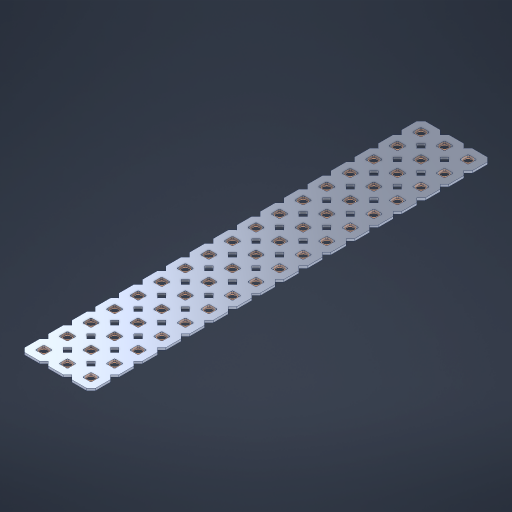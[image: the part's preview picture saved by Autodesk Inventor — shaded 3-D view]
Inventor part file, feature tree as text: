
AUTODESK INVENTOR PART (.ipt)
format: ipt  version: 2023 (Build 270158000, 158)  size: 847,872 bytes
history: native  units: in
note: dims shown in document units (in); Inventor stores cm internally (conversion verified against a paired STEP export)
features: other x52, extrude x50, sketch x2, pattern_linear x1
ambient origin geometry x8: Origin, YZ Plane, XZ Plane, XY Plane, X Axis, Y Axis, Z Axis, Center Point
bodies: Solid1 (feature_tree), Body (feature_tree)
feature tree (105):
  pattern_linear  "Rectangular Pattern1"  Spacing1=0.09in  [1 undecoded]
  sketch  "Sketch1"  dims[d1=0.5in]
  sketch  "Sketch2"  dims[d2=0.182in d3=0.09in d4=0.09in d5=0.09in d6=0.09in d7=0.09in d8=0.09in d9=0.09in d10=0.09in d11=0.02in d13=0.0in d14=0.172in d15=0.0625in d16=0.0in d19=0.5in d22=0.5in]
  other  "Srf1"
  other  "Srf126"
  other  "Srf127"
  other  "Srf128"
  other  "Srf129"
  other  "Srf130"
  other  "Srf131"
  other  "Srf250"
  other  "Srf251"
  other  "Srf252"
  other  "Srf253"
  other  "Srf254"
  other  "Srf255"
  other  "Srf256"
  other  "Srf257"
  other  "Srf258"
  other  "Srf259"
  other  "Srf268"
  other  "Srf269"
  other  "Srf270"
  other  "Srf271"
  other  "Srf272"
  other  "Srf273"
  other  "Srf274"
  other  "Srf275"
  other  "Srf276"
  other  "Srf277"
  other  "Srf278"
  other  "Srf279"
  other  "Srf280"
  other  "Srf281"
  other  "Srf282"
  other  "Srf283"
  other  "Srf284"
  other  "Srf293"
  other  "Srf294"
  other  "Srf295"
  other  "Srf296"
  other  "Srf297"
  other  "Srf298"
  other  "Srf299"
  other  "Srf300"
  other  "Srf301"
  other  "Srf302"
  other  "Srf303"
  other  "Srf304"
  other  "Srf305"
  other  "Srf306"
  other  "Srf307"
  other  "Srf308"
  other  "Srf309"
  other  "Circle"
  extrude  "ExtrusionSrf126"  Depth=0.09in
  extrude  "ExtrusionSrf127"  Depth=0.09in
  extrude  "ExtrusionSrf128"  Depth=0.09in
  extrude  "ExtrusionSrf129"  Depth=0.09in
  extrude  "ExtrusionSrf130"  Depth=0.09in
  extrude  "ExtrusionSrf131"  Depth=0.09in
  extrude  "ExtrusionSrf250"  Depth=0.09in
  extrude  "ExtrusionSrf251"  Depth=0.02in
  extrude  "ExtrusionSrf252"  TaperAngle=0.0deg  [1 undecoded]
  extrude  "ExtrusionSrf253"  Depth=0.5in
  extrude  "ExtrusionSrf254"  Depth=0.5in TaperAngle=0.0deg
  extrude  "ExtrusionSrf255"  Depth=0.5in
  extrude  "ExtrusionSrf256"  Depth=0.5in
  extrude  "ExtrusionSrf257"  [1 undecoded]
  extrude  "ExtrusionSrf258"  [1 undecoded]
  extrude  "ExtrusionSrf259"  [1 undecoded]
  extrude  "ExtrusionSrf268"  [1 undecoded]
  extrude  "ExtrusionSrf269"  [1 undecoded]
  extrude  "ExtrusionSrf270"  [1 undecoded]
  extrude  "ExtrusionSrf271"  [1 undecoded]
  extrude  "ExtrusionSrf272"  [1 undecoded]
  extrude  "ExtrusionSrf273"  [1 undecoded]
  extrude  "ExtrusionSrf274"  [1 undecoded]
  extrude  "ExtrusionSrf275"  [1 undecoded]
  extrude  "ExtrusionSrf276"  [1 undecoded]
  extrude  "ExtrusionSrf277"  [1 undecoded]
  extrude  "ExtrusionSrf278"  [1 undecoded]
  extrude  "ExtrusionSrf279"  [1 undecoded]
  extrude  "ExtrusionSrf280"  [1 undecoded]
  extrude  "ExtrusionSrf281"  [1 undecoded]
  extrude  "ExtrusionSrf282"  [1 undecoded]
  extrude  "ExtrusionSrf283"  [1 undecoded]
  extrude  "ExtrusionSrf284"  [1 undecoded]
  extrude  "ExtrusionSrf293"  [1 undecoded]
  extrude  "ExtrusionSrf294"  [1 undecoded]
  extrude  "ExtrusionSrf295"  [1 undecoded]
  extrude  "ExtrusionSrf296"  [1 undecoded]
  extrude  "ExtrusionSrf297"  [1 undecoded]
  extrude  "ExtrusionSrf298"  [1 undecoded]
  extrude  "ExtrusionSrf299"  [1 undecoded]
  extrude  "ExtrusionSrf300"  [1 undecoded]
  extrude  "ExtrusionSrf301"  [1 undecoded]
  extrude  "ExtrusionSrf302"  [1 undecoded]
  extrude  "ExtrusionSrf303"  [1 undecoded]
  extrude  "ExtrusionSrf304"  [1 undecoded]
  extrude  "ExtrusionSrf305"  [1 undecoded]
  extrude  "ExtrusionSrf306"  [1 undecoded]
  extrude  "ExtrusionSrf307"  [1 undecoded]
  extrude  "ExtrusionSrf308"  [1 undecoded]
  extrude  "ExtrusionSrf309"  [1 undecoded]
note: 39 required parameter values undecoded (feature->parameter linkage not recoverable at this tier; creation-order binding heuristic only, values carry confidence <= 0.55)
